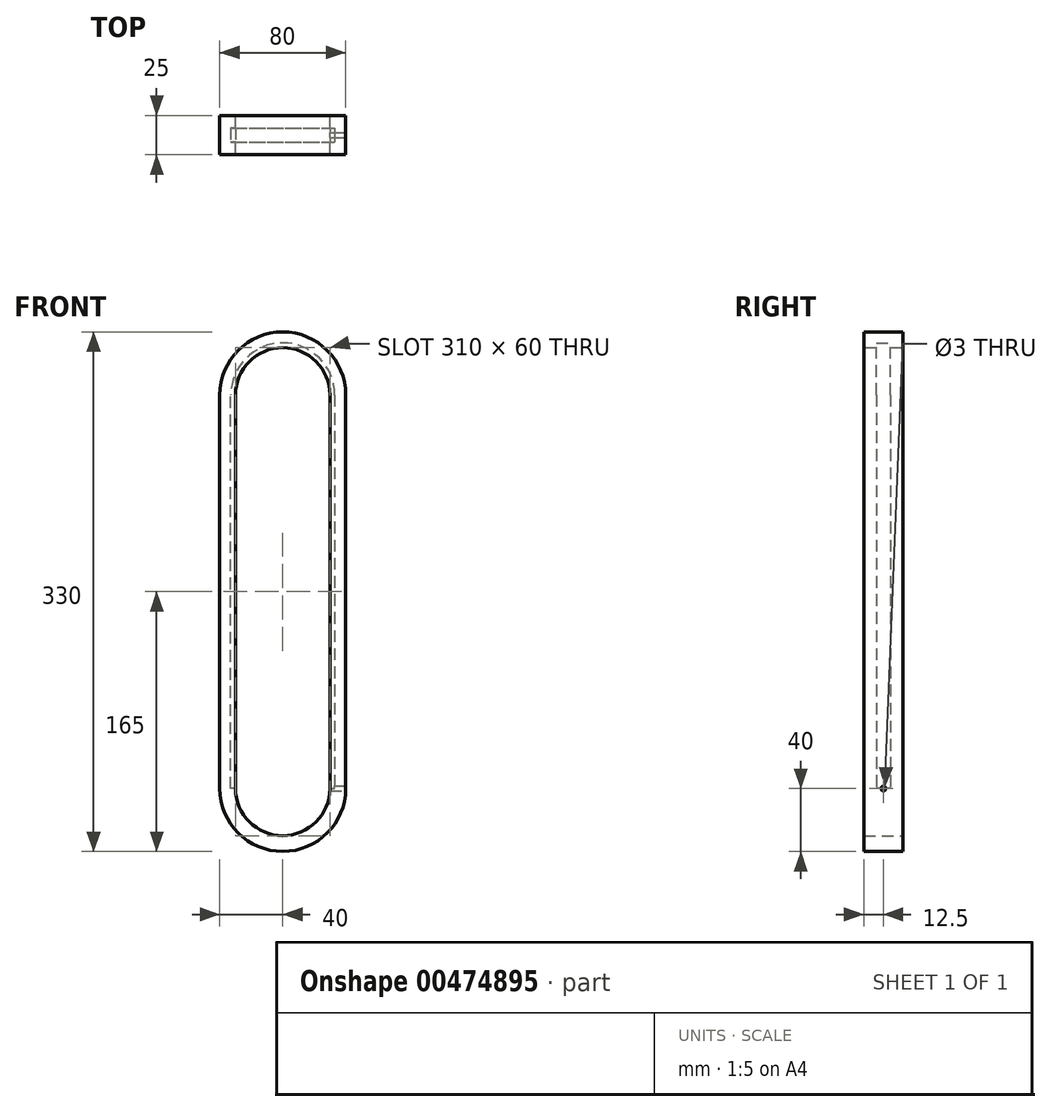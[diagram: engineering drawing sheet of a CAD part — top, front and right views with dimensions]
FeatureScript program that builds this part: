
annotation { "Feature Type Name" : "Feature", "Feature Type Description" : "" }
export const myFeature = defineFeature(function(context is Context, id is Id, definition is map)
    precondition{}
    {
        {
            var Q0;
            Q0=qCreatedBy(makeId("Front.planeOp"),FACE);
            var sketch = newSketch(context, id + "F0", { "sketchPlane" : qUnion([Q0])});
            skLineSegment(sketch, "E0.left", {"start": v(0, 0) * mm, "end": v(0, 250) * mm});
            skLineSegment(sketch, "E0.right", {"start": v(80, 0) * mm, "end": v(80, 250) * mm});
            skArc(sketch, "E1", {"start": v(80, 250) * mm, "mid": v(40, 290) * mm, "end": v(0, 250) * mm});
            skPoint(sketch, "E2.center.orphan", {"position": v(40, 0) * mm});
            skArc(sketch, "E3", {"start": v(0, 0) * mm, "mid": v(40, -40) * mm, "end": v(80, 0) * mm});
            skArc(sketch, "E4.0", {"start": v(70, 250) * mm, "mid": v(40, 280) * mm, "end": v(10, 250) * mm});
            skLineSegment(sketch, "E4.1", {"start": v(70, 0) * mm, "end": v(70, 250) * mm});
            skArc(sketch, "E4.2", {"start": v(10, 0) * mm, "mid": v(40, -30) * mm, "end": v(70, 0) * mm});
            skLineSegment(sketch, "E4.3", {"start": v(10, 0) * mm, "end": v(10, 250) * mm});
            skSolve(sketch);
        }
        {
            var Q0;
            Q0=qSketchRegion(id+"F0",true);
            extrude(context, id + "F1", {"entities" : qUnion([Q0]), "depth" : 25 * mm});
        }
        {
            var Q0;
            Q0=qCreatedBy(makeId("Top.planeOp"),FACE);
            var sketch = newSketch(context, id + "F2", { "sketchPlane" : qUnion([Q0])});
            skLineSegment(sketch, "E5.bottom", {"start": v(10, -8) * mm, "end": v(7, -8) * mm});
            skLineSegment(sketch, "E5.top", {"start": v(10, -17) * mm, "end": v(7, -17) * mm});
            skLineSegment(sketch, "E5.left", {"start": v(10, -8) * mm, "end": v(10, -17) * mm});
            skLineSegment(sketch, "E5.right", {"start": v(7, -8) * mm, "end": v(7, -17) * mm});
            skSolve(sketch);
        }
        {
            var Q0;
            Q0=makeQuery(id+"F2.imprint","IMPRINT",FACE,{"disambiguationData":[TD([[makeQuery(id+"F2.imprint","IMPRINT",EDGE,{"derivedFrom":sQuery(id+"F2.wireOp",EDGE,"E5.bottom")}),1.0]])]});
            var Q1;
            Q1=makeQuery(id+"F1.opExtrude","CAP_EDGE",EDGE,{"disambiguationData":[OSD([sQuery(id+"F0.wireOp",EDGE,"E4.3")])],"isStart":false});
            var Q2;
            Q2=makeQuery(id+"F1.opExtrude","CAP_EDGE",EDGE,{"disambiguationData":[OSD([sQuery(id+"F0.wireOp",EDGE,"E4.0")])],"isStart":false});
            var Q3;
            Q3=makeQuery(id+"F1.opExtrude","CAP_EDGE",EDGE,{"disambiguationData":[OSD([sQuery(id+"F0.wireOp",EDGE,"E4.1")])],"isStart":false});
            sweep(context, id + "F3", {"operationType" : NewBodyOperationType.REMOVE, "profiles" : qUnion([Q0]), "path" : qUnion([Q1, Q2, Q3])});
        }
        {
            var Q0;
            Q0=makeQuery(id+"F1.opExtrude","SWEPT_FACE",FACE,{"disambiguationData":[OSD([sQuery(id+"F0.wireOp",EDGE,"E0.right")])]});
            var sketch = newSketch(context, id + "F4", { "sketchPlane" : qUnion([Q0])});
            skCircle(sketch, "E6", {"center": v(-12.5, 0) * mm, "radius": 1.5 * mm});
            skSolve(sketch);
        }
        {
            var Q0;
            Q0=qSketchRegion(id+"F4",true);
            extrude(context, id + "F5", {"entities" : qUnion([Q0]), "operationType" : NewBodyOperationType.REMOVE, "endBound" : BoundingType.UP_TO_NEXT, "oppositeDirection" : true, "depth" : 25 * mm});
        }
    });
